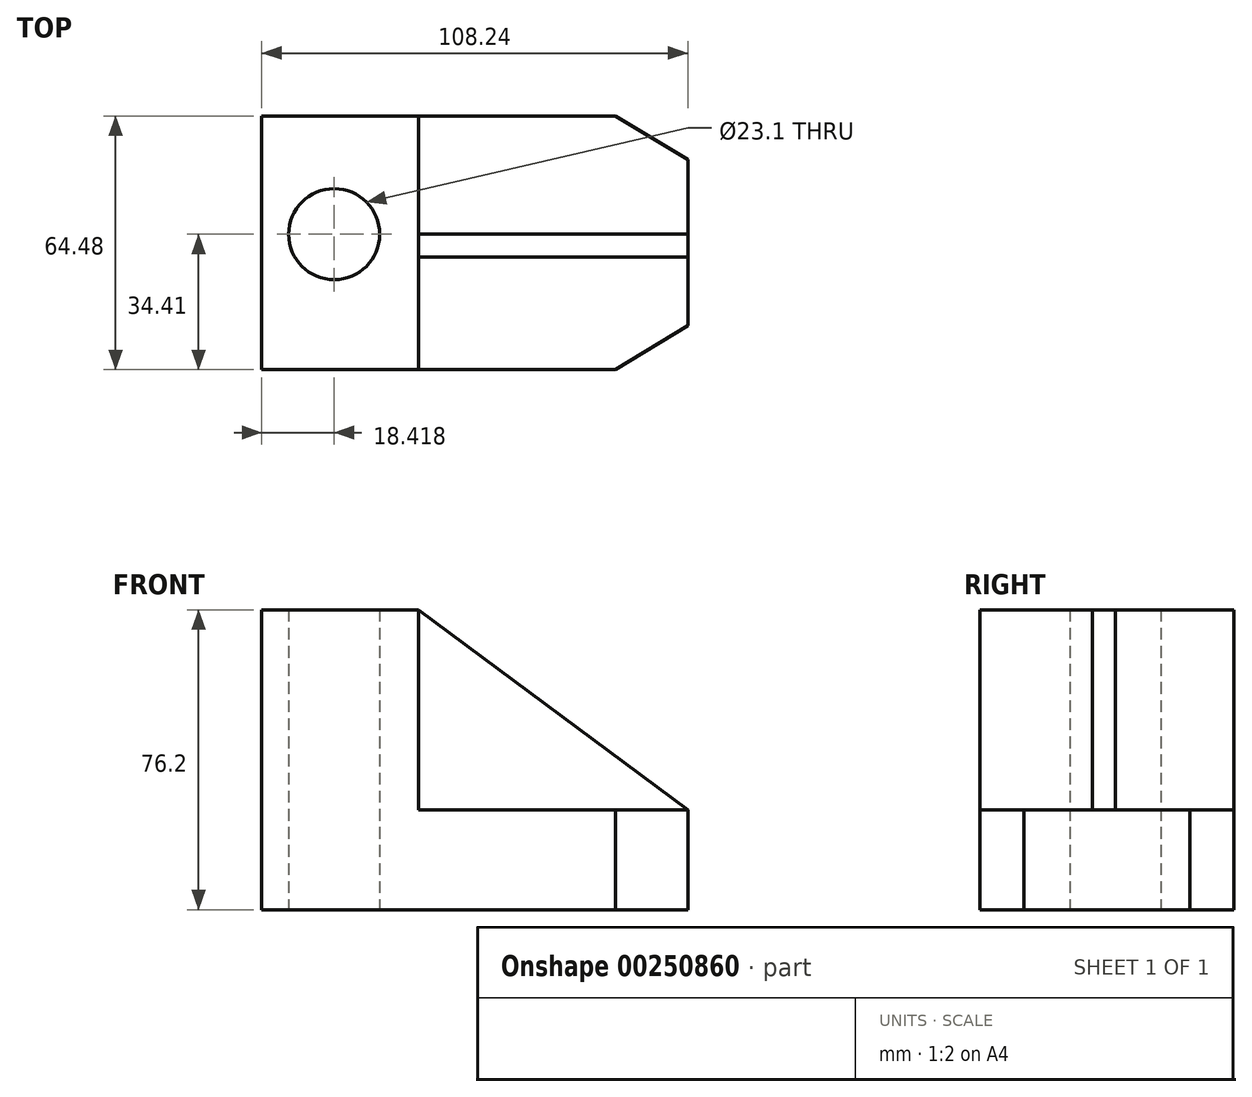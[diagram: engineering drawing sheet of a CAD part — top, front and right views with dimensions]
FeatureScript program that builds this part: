
annotation { "Feature Type Name" : "Feature", "Feature Type Description" : "" }
export const myFeature = defineFeature(function(context is Context, id is Id, definition is map)
    precondition{}
    {
        {
            var Q0;
            Q0=qCreatedBy(makeId("Top.planeOp"),FACE);
            var sketch = newSketch(context, id + "F0", { "sketchPlane" : qUnion([Q0])});
            skLineSegment(sketch, "E0.bottom", {"start": v(-48.56, 30.07) * mm, "end": v(41.33, 30.07) * mm});
            skLineSegment(sketch, "E0.top", {"start": v(-48.56, -34.4) * mm, "end": v(41.33, -34.4) * mm});
            skLineSegment(sketch, "E0.left", {"start": v(-48.56, 30.07) * mm, "end": v(-48.56, -34.4) * mm});
            skLineSegment(sketch, "E0.right", {"start": v(59.68, 18.92) * mm, "end": v(59.68, -23.26) * mm});
            skLineSegment(sketch, "E1", {"start": v(-8.76, 30.07) * mm, "end": v(-8.76, -34.4) * mm});
            skPoint(sketch, "E1.endSnap0", {"position": v(5.56, -34.4) * mm});
            skCircle(sketch, "E2", {"center": v(-30.14, 0) * mm, "radius": 11.55 * mm});
            skLineSegment(sketch, "E3", {"start": v(41.33, 30.07) * mm, "end": v(59.68, 18.92) * mm});
            skLineSegment(sketch, "E4.MirrorCS", {"start": v(41.33, -34.4) * mm, "end": v(59.68, -23.26) * mm});
            skLineSegment(sketch, "E5.MirrorCS", {"start": v(59.68, -23.26) * mm, "end": v(59.68, 18.92) * mm});
            skPoint(sketch, "E6.orphan", {"position": v(59.68, -34.4) * mm});
            skLineSegment(sketch, "E7", {"start": v(59.68, -5.75) * mm, "end": v(-10.53, -5.75) * mm});
            skLineSegment(sketch, "E8", {"start": v(59.68, 0) * mm, "end": v(-8.76, 0) * mm});
            skSolve(sketch);
        }
        {
            var Q0;
            {var subQ5=sQuery(id+"F0.wireOp",EDGE,"E0.left");Q0=makeQuery(id+"F0.imprint","IMPRINT",FACE,{"disambiguationData":[TD([[makeQuery(id+"F0.imprint","IMPRINT",EDGE,{"derivedFrom":subQ5}),1.0]])]});}
            extrude(context, id + "F1", {"entities" : qUnion([Q0]), "depth" : 76.2 * mm});
        }
        {
            var Q0;
            {var subQ3=sQuery(id+"F0.wireOp",EDGE,"E4.MirrorCS");Q0=makeQuery(id+"F0.imprint","IMPRINT",FACE,{"disambiguationData":[TD([[makeQuery(id+"F0.imprint","IMPRINT",EDGE,{"derivedFrom":subQ3}),1.0]])]});}
            extrude(context, id + "F2", {"entities" : qUnion([Q0]), "operationType" : NewBodyOperationType.ADD, "depth" : 25.4 * mm});
        }
        {
            var Q0;
            {var subQ1=sQuery(id+"F0.wireOp",EDGE,"E3");Q0=makeQuery(id+"F0.imprint","IMPRINT",FACE,{"disambiguationData":[TD([[makeQuery(id+"F0.imprint","IMPRINT",EDGE,{"derivedFrom":subQ1}),-1.0]])]});}
            extrude(context, id + "F3", {"entities" : qUnion([Q0]), "operationType" : NewBodyOperationType.ADD, "depth" : 25.4 * mm});
        }
        {
            var Q0;
            {var subQ0=sQuery(id+"F0.wireOp",EDGE,"E8");Q0=makeQuery(id+"F0.imprint","IMPRINT",FACE,{"disambiguationData":[TD([[makeQuery(id+"F0.imprint","IMPRINT",EDGE,{"derivedFrom":subQ0}),1.0]])]});}
            extrude(context, id + "F4", {"entities" : qUnion([Q0]), "operationType" : NewBodyOperationType.ADD, "depth" : 76.2 * mm});
        }
        {
            var Q0;
            Q0=makeQuery(id+"F4.opExtrude","SWEPT_FACE",FACE,{"disambiguationData":[OSD([sQuery(id+"F0.wireOp",EDGE,"E7")])]});
            var sketch = newSketch(context, id + "F5", { "sketchPlane" : qUnion([Q0])});
            skLineSegment(sketch, "E9", {"start": v(-8.76, 76.2) * mm, "end": v(59.68, 25.4) * mm});
            skSolve(sketch);
        }
        {
            var Q0;
            Q0 = qSketchRegion(id + "F5", true);
            var Q1;
            Q1=makeQuery(id+"F5.imprint","IMPRINT",FACE,{"disambiguationData":[TD([[makeQuery(id+"F5.imprint","IMPRINT",EDGE,{"derivedFrom":sQuery(id+"F5.wireOp",EDGE,"E9")}),1.0]])]});
            extrude(context, id + "F6", {"entities" : qUnion([Q0, Q1]), "operationType" : NewBodyOperationType.REMOVE, "oppositeDirection" : true, "depth" : 25.4 * mm});
        }
    });
